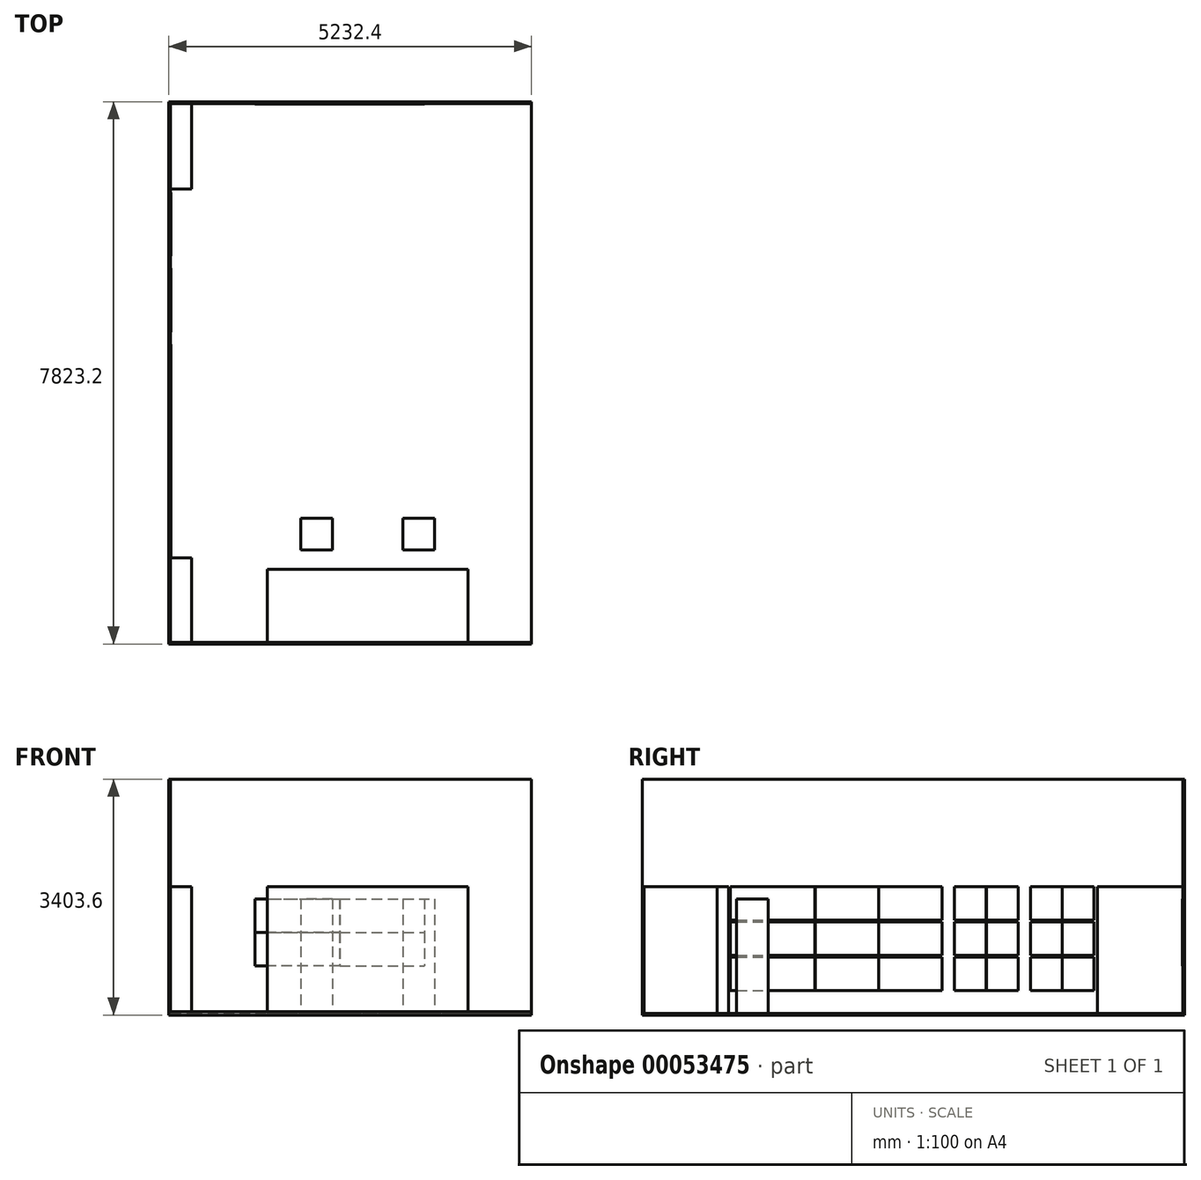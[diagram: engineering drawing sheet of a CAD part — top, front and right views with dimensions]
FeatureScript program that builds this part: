
annotation { "Feature Type Name" : "Feature", "Feature Type Description" : "" }
export const myFeature = defineFeature(function(context is Context, id is Id, definition is map)
    precondition{}
    {
        {
            var Q0;
            Q0=qCreatedBy(makeId("Right.planeOp"),FACE);
            var sketch = newSketch(context, id + "F0", { "sketchPlane" : qUnion([Q0])});
            skLineSegment(sketch, "E0.rect.bottom", {"start": v(3911.6, -1701.8) * mm, "end": v(-3911.6, -1701.8) * mm});
            skLineSegment(sketch, "E0.rect.top", {"start": v(3911.6, 1701.8) * mm, "end": v(-3911.6, 1701.8) * mm});
            skLineSegment(sketch, "E0.rect.left", {"start": v(3911.6, -1701.8) * mm, "end": v(3911.6, 1701.8) * mm});
            skLineSegment(sketch, "E0.rect.right", {"start": v(-3911.6, -1701.8) * mm, "end": v(-3911.6, 1701.8) * mm});
            skPoint(sketch, "E0.rect.middle", {"position": v(0, 0) * mm});
            skSolve(sketch);
        }
        {
            var Q0;
            Q0 = qSketchRegion(id + "F0", true);
            extrude(context, id + "F1", {"entities" : qUnion([Q0]), "depth" : 5232.4 * mm});
        }
        {
            var Q0;
            Q0=makeQuery(id+"F1.opExtrude","CAP_FACE",FACE,{"disambiguationData":[OSD([sQuery(id+"F0.wireOp",EDGE,"E0.rect.bottom"),sQuery(id+"F0.wireOp",EDGE,"E0.rect.top"),sQuery(id+"F0.wireOp",EDGE,"E0.rect.left"),sQuery(id+"F0.wireOp",EDGE,"E0.rect.right")])],"isStart":false});
            var sketch = newSketch(context, id + "F2", { "sketchPlane" : qUnion([Q0])});
            skLineSegment(sketch, "E1", {"start": v(3911.6, 1701.8) * mm, "end": v(3886.2, 1701.8) * mm});
            skLineSegment(sketch, "E2", {"start": v(3886.2, 1701.8) * mm, "end": v(3886.2, -1651) * mm});
            skLineSegment(sketch, "E3", {"start": v(3886.2, -1651) * mm, "end": v(-3911.6, -1651) * mm});
            skLineSegment(sketch, "E4", {"start": v(-3911.6, -1651) * mm, "end": v(-3911.6, -1701.8) * mm});
            skLineSegment(sketch, "E5", {"start": v(-3911.6, -1701.8) * mm, "end": v(-4512.2, -1701.8) * mm});
            skLineSegment(sketch, "E6", {"start": v(-4512.2, -1701.8) * mm, "end": v(-4512.2, 2212.08) * mm});
            skLineSegment(sketch, "E7", {"start": v(-4512.2, 2212.08) * mm, "end": v(3976.4, 2212.08) * mm});
            skLineSegment(sketch, "E8", {"start": v(3976.4, 2212.08) * mm, "end": v(3911.6, 1701.8) * mm});
            skSolve(sketch);
        }
        {
            var Q0;
            Q0 = qSketchRegion(id + "F2", true);
            extrude(context, id + "F3", {"entities" : qUnion([Q0]), "operationType" : NewBodyOperationType.REMOVE, "oppositeDirection" : true, "depth" : 5207 * mm});
        }
        {
            var Q0;
            Q0=makeQuery(id+"F3.boolean.opBoolean","COPY",FACE,{"derivedFrom":makeQuery(id+"F3.opExtrude","SWEPT_FACE",FACE,{"disambiguationData":[OSD([sQuery(id+"F2.wireOp",EDGE,"E3")])]})});
            var sketch = newSketch(context, id + "F4", { "sketchPlane" : qUnion([Q0])});
            skLineSegment(sketch, "E9", {"start": v(2628.9, -3886.2) * mm, "end": v(2628.9, 3886.2) * mm, "construction": true});
            skPoint(sketch, "E9.startSnap0", {"position": v(2628.9, 3886.2) * mm});
            skLineSegment(sketch, "E10", {"start": v(2628.9, -3886.2) * mm, "end": v(2628.9, -3911.6) * mm, "construction": true});
            skLineSegment(sketch, "E11.rect.bottom", {"start": v(25.4, 3886.2) * mm, "end": v(5232.4, 3886.2) * mm});
            skLineSegment(sketch, "E11.rect.top", {"start": v(25.4, -3886.2) * mm, "end": v(5232.4, -3886.2) * mm});
            skLineSegment(sketch, "E11.rect.left", {"start": v(25.4, 3886.2) * mm, "end": v(25.4, -3886.2) * mm});
            skLineSegment(sketch, "E11.rect.right", {"start": v(5232.4, 3886.2) * mm, "end": v(5232.4, -3886.2) * mm});
            skPoint(sketch, "E11.rect.middle", {"position": v(2628.9, 0) * mm});
            skSolve(sketch);
        }
        {
            var Q0;
            Q0 = qSketchRegion(id + "F4", true);
            extrude(context, id + "F5", {"entities" : qUnion([Q0]), "operationType" : NewBodyOperationType.REMOVE, "oppositeDirection" : true, "depth" : 25.4 * mm});
        }
        {
            var Q0;
            Q0=makeQuery(id+"F5.boolean.opBoolean","COPY",FACE,{"derivedFrom":makeQuery(id+"F5.opExtrude","CAP_FACE",FACE,{"disambiguationData":[OSD([sQuery(id+"F4.wireOp",EDGE,"E11.rect.bottom"),sQuery(id+"F4.wireOp",EDGE,"E11.rect.top"),sQuery(id+"F4.wireOp",EDGE,"E11.rect.left"),sQuery(id+"F4.wireOp",EDGE,"E11.rect.right")])],"isStart":false})});
            var sketch = newSketch(context, id + "F6", { "sketchPlane" : qUnion([Q0])});
            skLineSegment(sketch, "E12", {"start": v(5232.4, -3886.2) * mm, "end": v(4318, -3886.2) * mm, "construction": true});
            skLineSegment(sketch, "E13", {"start": v(4318, -3886.2) * mm, "end": v(5232.4, -3886.2) * mm, "construction": true});
            skLineSegment(sketch, "E14", {"start": v(4318, -3886.2) * mm, "end": v(1422.4, -3886.2) * mm, "construction": true});
            skLineSegment(sketch, "E15", {"start": v(4318, -3886.2) * mm, "end": v(4318, -2832.1) * mm});
            skLineSegment(sketch, "E16", {"start": v(4318, -2832.1) * mm, "end": v(1422.4, -2832.1) * mm});
            skLineSegment(sketch, "E17", {"start": v(1422.4, -2832.1) * mm, "end": v(1422.4, -3886.2) * mm});
            skLineSegment(sketch, "E18", {"start": v(4318, -3886.2) * mm, "end": v(1422.4, -3886.2) * mm});
            skSolve(sketch);
        }
        {
            var Q0;
            Q0 = qSketchRegion(id + "F6", true);
            extrude(context, id + "F7", {"entities" : qUnion([Q0]), "operationType" : NewBodyOperationType.ADD, "depth" : 1828.8 * mm});
        }
        {
            var Q0;
            Q0=makeQuery(id+"F5.boolean.opBoolean","MERGE",FACE,{"derivedFrom":[makeQuery(id+"F3.boolean.opBoolean","COPY",FACE,{"derivedFrom":makeQuery(id+"F3.opExtrude","CAP_FACE",FACE,{"disambiguationData":[OSD([sQuery(id+"F2.wireOp",EDGE,"E1"),sQuery(id+"F2.wireOp",EDGE,"E2"),sQuery(id+"F2.wireOp",EDGE,"E3"),sQuery(id+"F2.wireOp",EDGE,"E4"),sQuery(id+"F2.wireOp",EDGE,"E5"),sQuery(id+"F2.wireOp",EDGE,"E6"),sQuery(id+"F2.wireOp",EDGE,"E7"),sQuery(id+"F2.wireOp",EDGE,"E8")])],"isStart":false})}),makeQuery(id+"F5.opExtrude","SWEPT_FACE",FACE,{"disambiguationData":[OSD([sQuery(id+"F4.wireOp",EDGE,"E11.rect.left")])]})]});
            var sketch = newSketch(context, id + "F8", { "sketchPlane" : qUnion([Q0])});
            skLineSegment(sketch, "E19", {"start": v(-3886.2, -1676.4) * mm, "end": v(-3886.2, 152.4) * mm, "construction": true});
            skLineSegment(sketch, "E20", {"start": v(-3886.2, 152.4) * mm, "end": v(-2641.6, 152.4) * mm, "construction": true});
            skLineSegment(sketch, "E21.bottom", {"start": v(-2641.6, 152.4) * mm, "end": v(-1422.4, 152.4) * mm});
            skLineSegment(sketch, "E21.top", {"start": v(-2641.6, -330.2) * mm, "end": v(-1422.4, -330.2) * mm});
            skLineSegment(sketch, "E21.left", {"start": v(-2641.6, 152.4) * mm, "end": v(-2641.6, -330.2) * mm});
            skLineSegment(sketch, "E21.right", {"start": v(-1422.4, 152.4) * mm, "end": v(-1422.4, -330.2) * mm});
            skLineSegment(sketch, "E22", {"start": v(-2641.6, -330.2) * mm, "end": v(-2641.6, -355.6) * mm, "construction": true});
            skLineSegment(sketch, "E23.bottom", {"start": v(-2641.6, -355.6) * mm, "end": v(-1422.4, -355.6) * mm});
            skLineSegment(sketch, "E23.top", {"start": v(-2641.6, -838.2) * mm, "end": v(-1422.4, -838.2) * mm});
            skLineSegment(sketch, "E23.left", {"start": v(-2641.6, -355.6) * mm, "end": v(-2641.6, -838.2) * mm});
            skLineSegment(sketch, "E23.right", {"start": v(-1422.4, -355.6) * mm, "end": v(-1422.4, -838.2) * mm});
            skLineSegment(sketch, "E24", {"start": v(-2641.6, -838.2) * mm, "end": v(-2641.6, -863.6) * mm, "construction": true});
            skLineSegment(sketch, "E25.bottom", {"start": v(-2641.6, -863.6) * mm, "end": v(-1422.4, -863.6) * mm});
            skLineSegment(sketch, "E25.top", {"start": v(-2641.6, -1346.2) * mm, "end": v(-1422.4, -1346.2) * mm});
            skLineSegment(sketch, "E25.left", {"start": v(-2641.6, -863.6) * mm, "end": v(-2641.6, -1346.2) * mm});
            skLineSegment(sketch, "E25.right", {"start": v(-1422.4, -863.6) * mm, "end": v(-1422.4, -1346.2) * mm});
            skLineSegment(sketch, "E26", {"start": v(-1422.4, 152.4) * mm, "end": v(-1419.86, 152.4) * mm, "construction": true});
            skLineSegment(sketch, "E27", {"start": v(-1419.86, 152.4) * mm, "end": v(-1419.86, -330.2) * mm, "construction": true});
            skLineSegment(sketch, "E28", {"start": v(-1419.86, -330.2) * mm, "end": v(-1419.86, -355.6) * mm, "construction": true});
            skLineSegment(sketch, "E29", {"start": v(-1419.86, -355.6) * mm, "end": v(-1419.86, -838.2) * mm, "construction": true});
            skLineSegment(sketch, "E30", {"start": v(-1419.86, -838.2) * mm, "end": v(-1419.86, -863.6) * mm, "construction": true});
            skLineSegment(sketch, "E31", {"start": v(-1419.86, -863.6) * mm, "end": v(-1419.86, -1346.2) * mm, "construction": true});
            skLineSegment(sketch, "E32.bottom", {"start": v(-1419.86, 152.4) * mm, "end": v(-505.46, 152.4) * mm});
            skLineSegment(sketch, "E32.top", {"start": v(-1419.86, -330.2) * mm, "end": v(-505.46, -330.2) * mm});
            skLineSegment(sketch, "E32.left", {"start": v(-1419.86, 152.4) * mm, "end": v(-1419.86, -330.2) * mm});
            skLineSegment(sketch, "E32.right", {"start": v(-505.46, 152.4) * mm, "end": v(-505.46, -330.2) * mm});
            skLineSegment(sketch, "E33.bottom", {"start": v(-1419.86, -355.6) * mm, "end": v(-505.46, -355.6) * mm});
            skLineSegment(sketch, "E33.top", {"start": v(-1419.86, -838.2) * mm, "end": v(-505.46, -838.2) * mm});
            skLineSegment(sketch, "E33.left", {"start": v(-1419.86, -355.6) * mm, "end": v(-1419.86, -838.2) * mm});
            skLineSegment(sketch, "E33.right", {"start": v(-505.46, -355.6) * mm, "end": v(-505.46, -838.2) * mm});
            skLineSegment(sketch, "E34.bottom", {"start": v(-1419.86, -863.6) * mm, "end": v(-505.46, -863.6) * mm});
            skLineSegment(sketch, "E34.top", {"start": v(-1419.86, -1346.2) * mm, "end": v(-505.46, -1346.2) * mm});
            skLineSegment(sketch, "E34.left", {"start": v(-1419.86, -863.6) * mm, "end": v(-1419.86, -1346.2) * mm});
            skLineSegment(sketch, "E34.right", {"start": v(-505.46, -863.6) * mm, "end": v(-505.46, -1346.2) * mm});
            skLineSegment(sketch, "E35", {"start": v(-505.46, 152.4) * mm, "end": v(-502.92, 152.4) * mm, "construction": true});
            skLineSegment(sketch, "E36.bottom", {"start": v(-502.92, 152.4) * mm, "end": v(411.48, 152.4) * mm});
            skLineSegment(sketch, "E36.top", {"start": v(-502.92, -330.2) * mm, "end": v(411.48, -330.2) * mm});
            skLineSegment(sketch, "E36.left", {"start": v(-502.92, 152.4) * mm, "end": v(-502.92, -330.2) * mm});
            skLineSegment(sketch, "E36.right", {"start": v(411.48, 152.4) * mm, "end": v(411.48, -330.2) * mm});
            skLineSegment(sketch, "E37", {"start": v(-502.92, -330.2) * mm, "end": v(-502.92, -355.6) * mm, "construction": true});
            skLineSegment(sketch, "E38.bottom", {"start": v(-502.92, -355.6) * mm, "end": v(411.48, -355.6) * mm});
            skLineSegment(sketch, "E38.top", {"start": v(-502.92, -838.2) * mm, "end": v(411.48, -838.2) * mm});
            skLineSegment(sketch, "E38.left", {"start": v(-502.92, -355.6) * mm, "end": v(-502.92, -838.2) * mm});
            skLineSegment(sketch, "E38.right", {"start": v(411.48, -355.6) * mm, "end": v(411.48, -838.2) * mm});
            skLineSegment(sketch, "E39", {"start": v(-502.92, -838.2) * mm, "end": v(-502.92, -863.6) * mm, "construction": true});
            skLineSegment(sketch, "E40.bottom", {"start": v(-502.92, -863.6) * mm, "end": v(411.48, -863.6) * mm});
            skLineSegment(sketch, "E40.top", {"start": v(-502.92, -1346.2) * mm, "end": v(411.48, -1346.2) * mm});
            skLineSegment(sketch, "E40.left", {"start": v(-502.92, -863.6) * mm, "end": v(-502.92, -1346.2) * mm});
            skLineSegment(sketch, "E40.right", {"start": v(411.48, -863.6) * mm, "end": v(411.48, -1346.2) * mm});
            skSolve(sketch);
        }
        {
            var Q0;
            Q0 = qSketchRegion(id + "F8", true);
            extrude(context, id + "F9", {"entities" : qUnion([Q0]), "operationType" : NewBodyOperationType.ADD, "depth" : 6.35 * mm});
        }
        {
            var Q0;
            Q0=makeQuery(id+"F5.boolean.opBoolean","MERGE",FACE,{"derivedFrom":[makeQuery(id+"F3.boolean.opBoolean","COPY",FACE,{"derivedFrom":makeQuery(id+"F3.opExtrude","CAP_FACE",FACE,{"disambiguationData":[OSD([sQuery(id+"F2.wireOp",EDGE,"E1"),sQuery(id+"F2.wireOp",EDGE,"E2"),sQuery(id+"F2.wireOp",EDGE,"E3"),sQuery(id+"F2.wireOp",EDGE,"E4"),sQuery(id+"F2.wireOp",EDGE,"E5"),sQuery(id+"F2.wireOp",EDGE,"E6"),sQuery(id+"F2.wireOp",EDGE,"E7"),sQuery(id+"F2.wireOp",EDGE,"E8")])],"isStart":false})}),makeQuery(id+"F5.opExtrude","SWEPT_FACE",FACE,{"disambiguationData":[OSD([sQuery(id+"F4.wireOp",EDGE,"E11.rect.left")])]})]});
            var sketch = newSketch(context, id + "F10", { "sketchPlane" : qUnion([Q0])});
            skLineSegment(sketch, "E41", {"start": v(411.48, 152.4) * mm, "end": v(589.28, 152.4) * mm, "construction": true});
            skLineSegment(sketch, "E42.bottom", {"start": v(589.28, 152.4) * mm, "end": v(1046.48, 152.4) * mm});
            skLineSegment(sketch, "E42.top", {"start": v(589.28, -330.2) * mm, "end": v(1046.48, -330.2) * mm});
            skLineSegment(sketch, "E42.left", {"start": v(589.28, 152.4) * mm, "end": v(589.28, -330.2) * mm});
            skLineSegment(sketch, "E42.right", {"start": v(1046.48, 152.4) * mm, "end": v(1046.48, -330.2) * mm});
            skLineSegment(sketch, "E43", {"start": v(1046.48, -330.2) * mm, "end": v(1046.48, -355.6) * mm, "construction": true});
            skLineSegment(sketch, "E44.bottom", {"start": v(1046.48, -355.6) * mm, "end": v(589.28, -355.6) * mm});
            skLineSegment(sketch, "E44.top", {"start": v(1046.48, -838.2) * mm, "end": v(589.28, -838.2) * mm});
            skLineSegment(sketch, "E44.left", {"start": v(1046.48, -355.6) * mm, "end": v(1046.48, -838.2) * mm});
            skLineSegment(sketch, "E44.right", {"start": v(589.28, -355.6) * mm, "end": v(589.28, -838.2) * mm});
            skLineSegment(sketch, "E45", {"start": v(1046.48, -838.2) * mm, "end": v(1046.48, -863.6) * mm, "construction": true});
            skLineSegment(sketch, "E46.bottom", {"start": v(1046.48, -863.6) * mm, "end": v(589.28, -863.6) * mm});
            skLineSegment(sketch, "E46.top", {"start": v(1046.48, -1346.2) * mm, "end": v(589.28, -1346.2) * mm});
            skLineSegment(sketch, "E46.left", {"start": v(1046.48, -863.6) * mm, "end": v(1046.48, -1346.2) * mm});
            skLineSegment(sketch, "E46.right", {"start": v(589.28, -863.6) * mm, "end": v(589.28, -1346.2) * mm});
            skLineSegment(sketch, "E47", {"start": v(1046.48, -1346.2) * mm, "end": v(1049.02, -1346.2) * mm, "construction": true});
            skLineSegment(sketch, "E48", {"start": v(1049.02, -1346.2) * mm, "end": v(1049.02, -863.6) * mm, "construction": true});
            skLineSegment(sketch, "E49", {"start": v(1049.02, -863.6) * mm, "end": v(1049.02, -838.2) * mm, "construction": true});
            skLineSegment(sketch, "E50", {"start": v(1049.02, -838.2) * mm, "end": v(1049.02, -355.6) * mm, "construction": true});
            skLineSegment(sketch, "E51", {"start": v(1049.02, -355.6) * mm, "end": v(1049.02, -330.2) * mm, "construction": true});
            skLineSegment(sketch, "E52", {"start": v(1049.02, -330.2) * mm, "end": v(1049.02, 152.4) * mm, "construction": true});
            skLineSegment(sketch, "E53.bottom", {"start": v(1049.02, 152.4) * mm, "end": v(1506.22, 152.4) * mm});
            skLineSegment(sketch, "E53.top", {"start": v(1049.02, -330.2) * mm, "end": v(1506.22, -330.2) * mm});
            skLineSegment(sketch, "E53.left", {"start": v(1049.02, 152.4) * mm, "end": v(1049.02, -330.2) * mm});
            skLineSegment(sketch, "E53.right", {"start": v(1506.22, 152.4) * mm, "end": v(1506.22, -330.2) * mm});
            skLineSegment(sketch, "E54.bottom", {"start": v(1049.02, -355.6) * mm, "end": v(1506.22, -355.6) * mm});
            skLineSegment(sketch, "E54.top", {"start": v(1049.02, -838.2) * mm, "end": v(1506.22, -838.2) * mm});
            skLineSegment(sketch, "E54.left", {"start": v(1049.02, -355.6) * mm, "end": v(1049.02, -838.2) * mm});
            skLineSegment(sketch, "E54.right", {"start": v(1506.22, -355.6) * mm, "end": v(1506.22, -838.2) * mm});
            skLineSegment(sketch, "E55.bottom", {"start": v(1049.02, -863.6) * mm, "end": v(1506.22, -863.6) * mm});
            skLineSegment(sketch, "E55.top", {"start": v(1049.02, -1346.2) * mm, "end": v(1506.22, -1346.2) * mm});
            skLineSegment(sketch, "E55.left", {"start": v(1049.02, -863.6) * mm, "end": v(1049.02, -1346.2) * mm});
            skLineSegment(sketch, "E55.right", {"start": v(1506.22, -863.6) * mm, "end": v(1506.22, -1346.2) * mm});
            skLineSegment(sketch, "E56", {"start": v(1506.22, 152.4) * mm, "end": v(1684.02, 152.4) * mm, "construction": true});
            skLineSegment(sketch, "E57.bottom", {"start": v(1684.02, 152.4) * mm, "end": v(2141.22, 152.4) * mm});
            skLineSegment(sketch, "E57.top", {"start": v(1684.02, -330.2) * mm, "end": v(2141.22, -330.2) * mm});
            skLineSegment(sketch, "E57.left", {"start": v(1684.02, 152.4) * mm, "end": v(1684.02, -330.2) * mm});
            skLineSegment(sketch, "E57.right", {"start": v(2141.22, 152.4) * mm, "end": v(2141.22, -330.2) * mm});
            skLineSegment(sketch, "E58", {"start": v(1506.22, -355.6) * mm, "end": v(1684.02, -355.6) * mm, "construction": true});
            skLineSegment(sketch, "E59", {"start": v(1684.02, -355.6) * mm, "end": v(1684.02, -838.2) * mm, "construction": true});
            skLineSegment(sketch, "E60", {"start": v(1684.02, -838.2) * mm, "end": v(1684.02, -863.6) * mm, "construction": true});
            skLineSegment(sketch, "E61", {"start": v(1684.02, -863.6) * mm, "end": v(1684.02, -1346.2) * mm, "construction": true});
            skLineSegment(sketch, "E62.bottom", {"start": v(1684.02, -355.6) * mm, "end": v(2141.22, -355.6) * mm});
            skLineSegment(sketch, "E62.top", {"start": v(1684.02, -838.2) * mm, "end": v(2141.22, -838.2) * mm});
            skLineSegment(sketch, "E62.left", {"start": v(1684.02, -355.6) * mm, "end": v(1684.02, -838.2) * mm});
            skLineSegment(sketch, "E62.right", {"start": v(2141.22, -355.6) * mm, "end": v(2141.22, -838.2) * mm});
            skLineSegment(sketch, "E63.bottom", {"start": v(1684.02, -863.6) * mm, "end": v(2141.22, -863.6) * mm});
            skLineSegment(sketch, "E63.top", {"start": v(1684.02, -1346.2) * mm, "end": v(2141.22, -1346.2) * mm});
            skLineSegment(sketch, "E63.left", {"start": v(1684.02, -863.6) * mm, "end": v(1684.02, -1346.2) * mm});
            skLineSegment(sketch, "E63.right", {"start": v(2141.22, -863.6) * mm, "end": v(2141.22, -1346.2) * mm});
            skLineSegment(sketch, "E64", {"start": v(2141.22, -1346.2) * mm, "end": v(2143.76, -1346.2) * mm, "construction": true});
            skLineSegment(sketch, "E65", {"start": v(2143.76, -1346.2) * mm, "end": v(2143.76, -863.6) * mm, "construction": true});
            skLineSegment(sketch, "E66", {"start": v(2143.76, -863.6) * mm, "end": v(2143.76, -838.2) * mm, "construction": true});
            skLineSegment(sketch, "E67", {"start": v(2143.76, -838.2) * mm, "end": v(2143.76, -355.6) * mm, "construction": true});
            skLineSegment(sketch, "E68", {"start": v(2143.76, -355.6) * mm, "end": v(2143.76, -330.2) * mm, "construction": true});
            skLineSegment(sketch, "E69", {"start": v(2143.76, -330.2) * mm, "end": v(2143.76, 152.4) * mm, "construction": true});
            skLineSegment(sketch, "E70.bottom", {"start": v(2143.76, 152.4) * mm, "end": v(2600.96, 152.4) * mm});
            skLineSegment(sketch, "E70.top", {"start": v(2143.76, -330.2) * mm, "end": v(2600.96, -330.2) * mm});
            skLineSegment(sketch, "E70.left", {"start": v(2143.76, 152.4) * mm, "end": v(2143.76, -330.2) * mm});
            skLineSegment(sketch, "E70.right", {"start": v(2600.96, 152.4) * mm, "end": v(2600.96, -330.2) * mm});
            skLineSegment(sketch, "E71.bottom", {"start": v(2143.76, -355.6) * mm, "end": v(2600.96, -355.6) * mm});
            skLineSegment(sketch, "E71.top", {"start": v(2143.76, -838.2) * mm, "end": v(2600.96, -838.2) * mm});
            skLineSegment(sketch, "E71.left", {"start": v(2143.76, -355.6) * mm, "end": v(2143.76, -838.2) * mm});
            skLineSegment(sketch, "E71.right", {"start": v(2600.96, -355.6) * mm, "end": v(2600.96, -838.2) * mm});
            skLineSegment(sketch, "E72.bottom", {"start": v(2143.76, -863.6) * mm, "end": v(2600.96, -863.6) * mm});
            skLineSegment(sketch, "E72.top", {"start": v(2143.76, -1346.2) * mm, "end": v(2600.96, -1346.2) * mm});
            skLineSegment(sketch, "E72.left", {"start": v(2143.76, -863.6) * mm, "end": v(2143.76, -1346.2) * mm});
            skLineSegment(sketch, "E72.right", {"start": v(2600.96, -863.6) * mm, "end": v(2600.96, -1346.2) * mm});
            skLineSegment(sketch, "E73", {"start": v(2600.96, 152.4) * mm, "end": v(3886.2, 152.4) * mm, "construction": true});
            skSolve(sketch);
        }
        {
            var Q0;
            Q0 = qSketchRegion(id + "F10", true);
            extrude(context, id + "F11", {"entities" : qUnion([Q0]), "operationType" : NewBodyOperationType.ADD, "depth" : 6.35 * mm});
        }
        {
            var Q0;
            Q0=makeQuery(id+"F5.boolean.opBoolean","MERGE",FACE,{"derivedFrom":[makeQuery(id+"F3.boolean.opBoolean","COPY",FACE,{"derivedFrom":makeQuery(id+"F3.opExtrude","SWEPT_FACE",FACE,{"disambiguationData":[OSD([sQuery(id+"F2.wireOp",EDGE,"E2")])]})}),makeQuery(id+"F5.opExtrude","SWEPT_FACE",FACE,{"disambiguationData":[OSD([sQuery(id+"F4.wireOp",EDGE,"E11.rect.bottom")])]})]});
            var sketch = newSketch(context, id + "F12", { "sketchPlane" : qUnion([Q0])});
            skLineSegment(sketch, "E74", {"start": v(25.4, -1676.4) * mm, "end": v(25.4, -25.4) * mm, "construction": true});
            skLineSegment(sketch, "E75", {"start": v(25.4, -25.4) * mm, "end": v(1244.6, -25.4) * mm, "construction": true});
            skLineSegment(sketch, "E76", {"start": v(1244.6, -25.4) * mm, "end": v(2463.8, -25.4) * mm, "construction": true});
            skLineSegment(sketch, "E77", {"start": v(2463.8, -25.4) * mm, "end": v(2466.34, -25.4) * mm, "construction": true});
            skLineSegment(sketch, "E78", {"start": v(2466.34, -25.4) * mm, "end": v(3685.54, -25.4) * mm, "construction": true});
            skLineSegment(sketch, "E79.bottom", {"start": v(1244.6, -25.4) * mm, "end": v(2463.8, -25.4) * mm});
            skLineSegment(sketch, "E79.top", {"start": v(1244.6, -508) * mm, "end": v(2463.8, -508) * mm});
            skLineSegment(sketch, "E79.left", {"start": v(1244.6, -25.4) * mm, "end": v(1244.6, -508) * mm});
            skLineSegment(sketch, "E79.right", {"start": v(2463.8, -25.4) * mm, "end": v(2463.8, -508) * mm});
            skLineSegment(sketch, "E80.bottom", {"start": v(2466.34, -25.4) * mm, "end": v(3685.54, -25.4) * mm});
            skLineSegment(sketch, "E80.top", {"start": v(2466.34, -508) * mm, "end": v(3685.54, -508) * mm});
            skLineSegment(sketch, "E80.left", {"start": v(2466.34, -25.4) * mm, "end": v(2466.34, -508) * mm});
            skLineSegment(sketch, "E80.right", {"start": v(3685.54, -25.4) * mm, "end": v(3685.54, -508) * mm});
            skLineSegment(sketch, "E81", {"start": v(2463.8, -508) * mm, "end": v(2463.8, -508) * mm});
            skLineSegment(sketch, "E82", {"start": v(2463.8, -508) * mm, "end": v(2463.8, -510.54) * mm, "construction": true});
            skLineSegment(sketch, "E83", {"start": v(2463.8, -510.54) * mm, "end": v(2463.8, -510.54) * mm});
            skLineSegment(sketch, "E84.bottom", {"start": v(2463.8, -510.54) * mm, "end": v(1244.6, -510.54) * mm});
            skLineSegment(sketch, "E84.top", {"start": v(2463.8, -993.14) * mm, "end": v(1244.6, -993.14) * mm});
            skLineSegment(sketch, "E84.left", {"start": v(2463.8, -510.54) * mm, "end": v(2463.8, -993.14) * mm});
            skLineSegment(sketch, "E84.right", {"start": v(1244.6, -510.54) * mm, "end": v(1244.6, -993.14) * mm});
            skLineSegment(sketch, "E85", {"start": v(2463.8, -510.54) * mm, "end": v(2466.34, -510.54) * mm, "construction": true});
            skLineSegment(sketch, "E86.bottom", {"start": v(2466.34, -510.54) * mm, "end": v(3685.54, -510.54) * mm});
            skLineSegment(sketch, "E86.top", {"start": v(2466.34, -993.14) * mm, "end": v(3685.54, -993.14) * mm});
            skLineSegment(sketch, "E86.left", {"start": v(2466.34, -510.54) * mm, "end": v(2466.34, -993.14) * mm});
            skLineSegment(sketch, "E86.right", {"start": v(3685.54, -510.54) * mm, "end": v(3685.54, -993.14) * mm});
            skSolve(sketch);
        }
        {
            var Q0;
            Q0 = qSketchRegion(id + "F12", true);
            extrude(context, id + "F13", {"entities" : qUnion([Q0]), "operationType" : NewBodyOperationType.ADD, "depth" : 6.35 * mm});
        }
        {
            var Q0;
            Q0=makeQuery(id+"F5.boolean.opBoolean","COPY",FACE,{"derivedFrom":makeQuery(id+"F5.opExtrude","CAP_FACE",FACE,{"disambiguationData":[OSD([sQuery(id+"F4.wireOp",EDGE,"E11.rect.bottom"),sQuery(id+"F4.wireOp",EDGE,"E11.rect.top"),sQuery(id+"F4.wireOp",EDGE,"E11.rect.left"),sQuery(id+"F4.wireOp",EDGE,"E11.rect.right")])],"isStart":false})});
            var sketch = newSketch(context, id + "F14", { "sketchPlane" : qUnion([Q0])});
            skLineSegment(sketch, "E87.bottom", {"start": v(25.4, 3886.2) * mm, "end": v(330.2, 3886.2) * mm});
            skLineSegment(sketch, "E87.top", {"start": v(25.4, 2654.3) * mm, "end": v(330.2, 2654.3) * mm});
            skLineSegment(sketch, "E87.left", {"start": v(25.4, 3886.2) * mm, "end": v(25.4, 2654.3) * mm});
            skLineSegment(sketch, "E87.right", {"start": v(330.2, 3886.2) * mm, "end": v(330.2, 2654.3) * mm});
            skSolve(sketch);
        }
        {
            var Q0;
            Q0 = qSketchRegion(id + "F14", true);
            extrude(context, id + "F15", {"entities" : qUnion([Q0]), "operationType" : NewBodyOperationType.ADD, "depth" : 1828.8 * mm});
        }
        {
            var Q0;
            Q0=makeQuery(id+"F5.boolean.opBoolean","COPY",FACE,{"derivedFrom":makeQuery(id+"F5.opExtrude","CAP_FACE",FACE,{"disambiguationData":[OSD([sQuery(id+"F4.wireOp",EDGE,"E11.rect.bottom"),sQuery(id+"F4.wireOp",EDGE,"E11.rect.top"),sQuery(id+"F4.wireOp",EDGE,"E11.rect.left"),sQuery(id+"F4.wireOp",EDGE,"E11.rect.right")])],"isStart":false})});
            var sketch = newSketch(context, id + "F16", { "sketchPlane" : qUnion([Q0])});
            skLineSegment(sketch, "E88.bottom", {"start": v(25.4, -3886.2) * mm, "end": v(330.2, -3886.2) * mm});
            skLineSegment(sketch, "E88.top", {"start": v(25.4, -2667) * mm, "end": v(330.2, -2667) * mm});
            skLineSegment(sketch, "E88.left", {"start": v(25.4, -3886.2) * mm, "end": v(25.4, -2667) * mm});
            skLineSegment(sketch, "E88.right", {"start": v(330.2, -3886.2) * mm, "end": v(330.2, -2667) * mm});
            skSolve(sketch);
        }
        {
            var Q0;
            Q0 = qSketchRegion(id + "F16", true);
            extrude(context, id + "F17", {"entities" : qUnion([Q0]), "operationType" : NewBodyOperationType.ADD, "depth" : 1828.8 * mm});
        }
        {
            var Q0;
            Q0=makeQuery(id+"F5.boolean.opBoolean","COPY",FACE,{"derivedFrom":makeQuery(id+"F5.opExtrude","CAP_FACE",FACE,{"disambiguationData":[OSD([sQuery(id+"F4.wireOp",EDGE,"E11.rect.bottom"),sQuery(id+"F4.wireOp",EDGE,"E11.rect.top"),sQuery(id+"F4.wireOp",EDGE,"E11.rect.left"),sQuery(id+"F4.wireOp",EDGE,"E11.rect.right")])],"isStart":false})});
            var sketch = newSketch(context, id + "F18", { "sketchPlane" : qUnion([Q0])});
            skLineSegment(sketch, "E89", {"start": v(2870.2, -2832.1) * mm, "end": v(2870.2, -2324.1) * mm, "construction": true});
            skLineSegment(sketch, "E90", {"start": v(2870.2, -2324.1) * mm, "end": v(2362.2, -2324.1) * mm, "construction": true});
            skLineSegment(sketch, "E91", {"start": v(2362.2, -2324.1) * mm, "end": v(2362.2, -2095.5) * mm, "construction": true});
            skLineSegment(sketch, "E92", {"start": v(2362.2, -2095.5) * mm, "end": v(3378.2, -2095.5) * mm, "construction": true});
            skLineSegment(sketch, "E93", {"start": v(3378.2, -2095.5) * mm, "end": v(3378.2, -2324.1) * mm, "construction": true});
            skLineSegment(sketch, "E94", {"start": v(3378.2, -2324.1) * mm, "end": v(2870.2, -2324.1) * mm, "construction": true});
            skLineSegment(sketch, "E95.bottom", {"start": v(2362.2, -2095.5) * mm, "end": v(1905, -2095.5) * mm});
            skLineSegment(sketch, "E95.top", {"start": v(2362.2, -2552.7) * mm, "end": v(1905, -2552.7) * mm});
            skLineSegment(sketch, "E95.left", {"start": v(2362.2, -2095.5) * mm, "end": v(2362.2, -2552.7) * mm});
            skLineSegment(sketch, "E95.right", {"start": v(1905, -2095.5) * mm, "end": v(1905, -2552.7) * mm});
            skLineSegment(sketch, "E96.bottom", {"start": v(3378.2, -2095.5) * mm, "end": v(3835.4, -2095.5) * mm});
            skLineSegment(sketch, "E96.top", {"start": v(3378.2, -2552.7) * mm, "end": v(3835.4, -2552.7) * mm});
            skLineSegment(sketch, "E96.left", {"start": v(3378.2, -2095.5) * mm, "end": v(3378.2, -2552.7) * mm});
            skLineSegment(sketch, "E96.right", {"start": v(3835.4, -2095.5) * mm, "end": v(3835.4, -2552.7) * mm});
            skSolve(sketch);
        }
        {
            var Q0;
            Q0 = qSketchRegion(id + "F18", true);
            extrude(context, id + "F19", {"entities" : qUnion([Q0]), "operationType" : NewBodyOperationType.ADD, "depth" : 1651 * mm});
        }
    });
